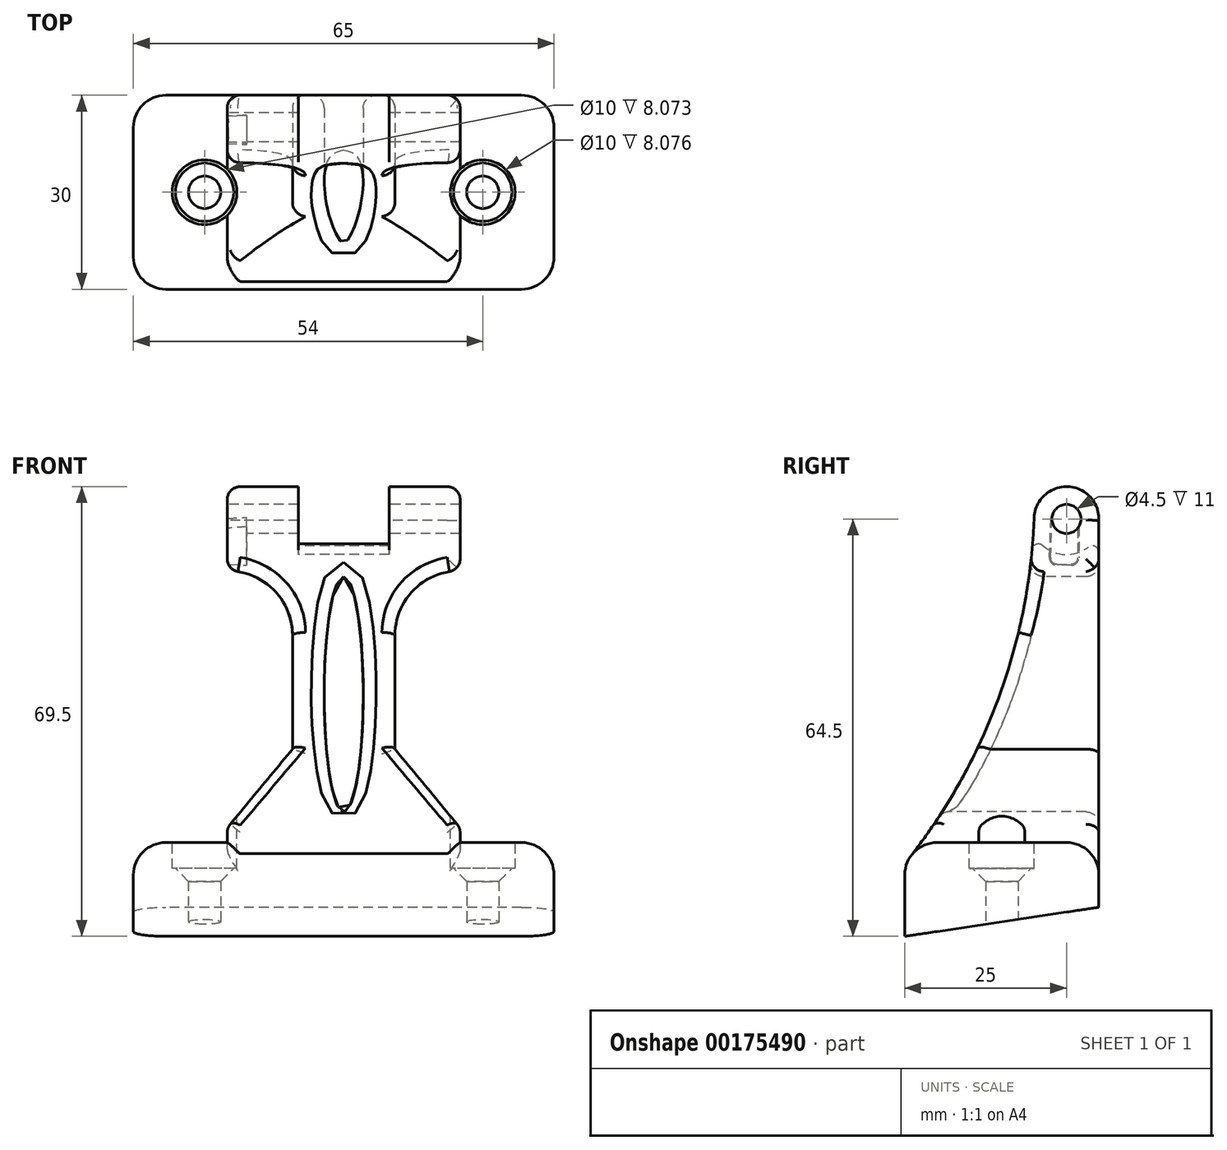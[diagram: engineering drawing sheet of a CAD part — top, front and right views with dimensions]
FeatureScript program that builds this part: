
annotation { "Feature Type Name" : "Feature", "Feature Type Description" : "" }
export const myFeature = defineFeature(function(context is Context, id is Id, definition is map)
    precondition{}
    {
        {
            var Q0;
            Q0=qCreatedBy(makeId("Top.planeOp"),FACE);
            var sketch = newSketch(context, id + "F0", { "sketchPlane" : qUnion([Q0])});
            skLineSegment(sketch, "E0.bottom", {"start": v(-27.5, 15) * mm, "end": v(27.5, 15) * mm});
            skLineSegment(sketch, "E0.top", {"start": v(-27.5, -15) * mm, "end": v(27.5, -15) * mm});
            skLineSegment(sketch, "E0.left", {"start": v(-32.5, 10) * mm, "end": v(-32.5, -10) * mm});
            skLineSegment(sketch, "E0.right", {"start": v(32.5, 10) * mm, "end": v(32.5, -10) * mm});
            skCircle(sketch, "E1", {"center": v(-21.5, 0) * mm, "radius": 2.5 * mm});
            skCircle(sketch, "E2.MirrorC", {"center": v(21.5, 0) * mm, "radius": 2.5 * mm});
            skPoint(sketch, "E3.visualSharp", {"position": v(-32.5, 15) * mm});
            skArc(sketch, "E3.filletArc", {"start": v(-27.5, 15) * mm, "mid": v(-31.04, 13.54) * mm, "end": v(-32.5, 10) * mm});
            skPoint(sketch, "E4.visualSharp", {"position": v(-32.5, -15) * mm});
            skArc(sketch, "E4.filletArc", {"start": v(-32.5, -10) * mm, "mid": v(-31.04, -13.54) * mm, "end": v(-27.5, -15) * mm});
            skPoint(sketch, "E5.visualSharp", {"position": v(32.5, -15) * mm});
            skArc(sketch, "E5.filletArc", {"start": v(27.5, -15) * mm, "mid": v(31.04, -13.54) * mm, "end": v(32.5, -10) * mm});
            skPoint(sketch, "E6.visualSharp", {"position": v(32.5, 15) * mm});
            skArc(sketch, "E6.filletArc", {"start": v(32.5, 10) * mm, "mid": v(31.04, 13.54) * mm, "end": v(27.5, 15) * mm});
            skSolve(sketch);
        }
        {
            var Q0;
            Q0 = qSketchRegion(id + "F0", true);
            extrude(context, id + "F1", {"entities" : qUnion([Q0]), "depth" : 10 * mm, "hasSecondDirection" : true, "secondDirectionOppositeDirection" : true, "secondDirectionDepth" : 5 * mm});
        }
        {
            var Q0;
            Q0=makeQuery(id+"F1.opExtrude","SWEPT_FACE",FACE,{"disambiguationData":[OSD([sQuery(id+"F0.wireOp",EDGE,"E0.left")])]});
            var sketch = newSketch(context, id + "F2", { "sketchPlane" : qUnion([Q0])});
            skLineSegment(sketch, "E7", {"start": v(15, -5) * mm, "end": v(-15, -5) * mm});
            skLineSegment(sketch, "E8", {"start": v(-15, -5) * mm, "end": v(-15, 0) * mm});
            skLineSegment(sketch, "E9", {"start": v(-15, 0) * mm, "end": v(15, -4.5) * mm});
            skLineSegment(sketch, "E10", {"start": v(15, -4.5) * mm, "end": v(15, -5) * mm});
            skSolve(sketch);
        }
        {
            var Q0;
            Q0 = qSketchRegion(id + "F2", true);
            extrude(context, id + "F3", {"entities" : qUnion([Q0]), "operationType" : NewBodyOperationType.REMOVE, "endBound" : BoundingType.THROUGH_ALL, "oppositeDirection" : true, "depth" : 25 * mm});
        }
        {
            var Q0;
            Q0=qCreatedBy(makeId("Right.planeOp"),FACE);
            var sketch = newSketch(context, id + "F4", { "sketchPlane" : qUnion([Q0])});
            skCircle(sketch, "E11", {"center": v(10, 60) * mm, "radius": 2.25 * mm});
            skCircle(sketch, "E12", {"center": v(10, 60) * mm, "radius": 5 * mm});
            skLineSegment(sketch, "E13", {"start": v(21.69, 10) * mm, "end": v(-30.08, 10) * mm, "construction": true});
            skLineSegment(sketch, "E14", {"start": v(15, 59.8) * mm, "end": v(15, 10) * mm});
            skArc(sketch, "E15", {"start": v(-12.48, 10) * mm, "mid": v(0.02, 33.78) * mm, "end": v(5, 60.19) * mm});
            skLineSegment(sketch, "E16", {"start": v(-12.48, 10) * mm, "end": v(15, 10) * mm});
            skSolve(sketch);
        }
        {
            var Q0;
            Q0 = qSketchRegion(id + "F4", true);
            extrude(context, id + "F5", {"entities" : qUnion([Q0]), "operationType" : NewBodyOperationType.ADD, "depth" : 18 * mm, "hasSecondDirection" : true, "secondDirectionOppositeDirection" : true, "secondDirectionDepth" : 18 * mm});
        }
        {
            var Q0;
            Q0=qCreatedBy(makeId("Right.planeOp"),FACE);
            var sketch = newSketch(context, id + "F6", { "sketchPlane" : qUnion([Q0])});
            skCircle(sketch, "E17", {"center": v(10, 60) * mm, "radius": 5.5 * mm});
            skSolve(sketch);
        }
        {
            var Q0;
            Q0 = qSketchRegion(id + "F6", true);
            extrude(context, id + "F7", {"entities" : qUnion([Q0]), "operationType" : NewBodyOperationType.REMOVE, "depth" : 7 * mm, "hasSecondDirection" : true, "secondDirectionOppositeDirection" : true, "secondDirectionDepth" : 7 * mm});
        }
        {
            var Q0;
            Q0=makeQuery(id+"F1.opExtrude","CAP_EDGE",EDGE,{"disambiguationData":[OSD([sQuery(id+"F0.wireOp",EDGE,"E0.right")])],"isStart":false});
            fillet(context, id + "F8", {"entities" : qUnion([Q0]), "radius" : 5 * mm, "tangentPropagation" : true, "allowEdgeOverflow" : false});
        }
        {
            var Q0;
            Q0=makeQuery(id+"F7.boolean.opBoolean","INTERSECT",EDGE,{"derivedFrom":[makeQuery(id+"F5.opExtrude","SWEPT_FACE",FACE,{"disambiguationData":[OSD([sQuery(id+"F4.wireOp",EDGE,"E15")])]}),makeQuery(id+"F7.opExtrude","SWEPT_FACE",FACE,{"disambiguationData":[OSD([sQuery(id+"F6.wireOp",EDGE,"E17")])]})]});
            var Q1;
            Q1=makeQuery(id+"F7.boolean.opBoolean","INTERSECT",EDGE,{"derivedFrom":[makeQuery(id+"F5.opExtrude","SWEPT_FACE",FACE,{"disambiguationData":[OSD([sQuery(id+"F4.wireOp",EDGE,"E14")])]}),makeQuery(id+"F7.opExtrude","SWEPT_FACE",FACE,{"disambiguationData":[OSD([sQuery(id+"F6.wireOp",EDGE,"E17")])]})]});
            fillet(context, id + "F9", {"entities" : qUnion([Q0, Q1]), "radius" : 1 * mm, "tangentPropagation" : true, "allowEdgeOverflow" : false});
        }
        {
            var Q0;
            Q0=makeQuery(id+"F5.opExtrude","CAP_FACE",FACE,{"disambiguationData":[OSD([sQuery(id+"F4.wireOp",EDGE,"E11"),sQuery(id+"F4.wireOp",EDGE,"E12"),sQuery(id+"F4.wireOp",EDGE,"E14"),sQuery(id+"F4.wireOp",EDGE,"E15"),sQuery(id+"F4.wireOp",EDGE,"E16")])],"isStart":true});
            var sketch = newSketch(context, id + "F10", { "sketchPlane" : qUnion([Q0])});
            skLineSegment(sketch, "E18", {"start": v(-7.75, 60.08) * mm, "end": v(-7.52, 54.04) * mm});
            skLineSegment(sketch, "E19", {"start": v(-11.75, 59.88) * mm, "end": v(-11.75, 54) * mm});
            skLineSegment(sketch, "E20", {"start": v(-10.75, 53) * mm, "end": v(-8.52, 53) * mm});
            skLineSegment(sketch, "E21", {"start": v(-7.75, 60.08) * mm, "end": v(-11.75, 59.88) * mm});
            skPoint(sketch, "E22.visualSharp", {"position": v(-11.75, 53) * mm});
            skArc(sketch, "E22.filletArc", {"start": v(-11.75, 54) * mm, "mid": v(-11.45, 53.3) * mm, "end": v(-10.75, 53) * mm});
            skPoint(sketch, "E23.visualSharp", {"position": v(-7.49, 53) * mm});
            skArc(sketch, "E23.filletArc", {"start": v(-8.52, 53) * mm, "mid": v(-7.8, 53.3) * mm, "end": v(-7.52, 54.04) * mm});
            skSolve(sketch);
        }
        {
            var Q0;
            Q0 = qSketchRegion(id + "F10", true);
            extrude(context, id + "F11", {"entities" : qUnion([Q0]), "operationType" : NewBodyOperationType.REMOVE, "oppositeDirection" : true, "depth" : 3 * mm, "hasDraft" : true, "draftAngle" : 3 * degree});
        }
        {
            var Q0;
            Q0=makeQuery(id+"Fu832J7Y8MEkpcE_1.opFillet","SPLIT",FACE,{"disambiguationData":[OD(1.0)],"derivedFrom":makeQuery(id+"F8.opFillet","SPLIT",FACE,{"disambiguationData":[OD(1.0)],"derivedFrom":makeQuery(id+"F1.opExtrude","CAP_FACE",FACE,{"disambiguationData":[OSD([sQuery(id+"F0.wireOp",EDGE,"E0.bottom"),sQuery(id+"F0.wireOp",EDGE,"E0.top"),sQuery(id+"F0.wireOp",EDGE,"E0.left"),sQuery(id+"F0.wireOp",EDGE,"E0.right"),sQuery(id+"F0.wireOp",EDGE,"E1"),sQuery(id+"F0.wireOp",EDGE,"E2.MirrorC"),sQuery(id+"F0.wireOp",EDGE,"E3.filletArc"),sQuery(id+"F0.wireOp",EDGE,"E4.filletArc"),sQuery(id+"F0.wireOp",EDGE,"E5.filletArc"),sQuery(id+"F0.wireOp",EDGE,"E6.filletArc")])],"isStart":false})})});
            var sketch = newSketch(context, id + "F12", { "sketchPlane" : qUnion([Q0])});
            skCircle(sketch, "E24", {"center": v(21.5, 0) * mm, "radius": 5 * mm});
            skCircle(sketch, "E25.MirrorC", {"center": v(-21.5, 0) * mm, "radius": 5 * mm});
            skSolve(sketch);
        }
        {
            var Q0;
            Q0 = qSketchRegion(id + "F12", true);
            extrude(context, id + "F13", {"entities" : qUnion([Q0]), "operationType" : NewBodyOperationType.REMOVE, "flatOperationType" : FlatOperationType.REMOVE, "oppositeDirection" : true, "offsetDistance" : 25 * mm, "depth" : 4 * mm, "hasSecondDirection" : true, "secondDirectionOppositeDirection" : false, "secondDirectionDepth" : 20 * mm, "domain" : OperationDomain.MODEL});
        }
        {
            var Q0;
            Q0=makeQuery(id+"F13.boolean.opBoolean","INTERSECT",EDGE,{"derivedFrom":[makeQuery(id+"F1.opExtrude","SWEPT_FACE",FACE,{"disambiguationData":[OSD([sQuery(id+"F0.wireOp",EDGE,"E1")])]}),makeQuery(id+"F13.opExtrude","CAP_FACE",FACE,{"disambiguationData":[OSD([sQuery(id+"F12.wireOp",EDGE,"E25.MirrorC")])],"isStart":false})]});
            var Q1;
            Q1=makeQuery(id+"F13.boolean.opBoolean","INTERSECT",EDGE,{"derivedFrom":[makeQuery(id+"F1.opExtrude","SWEPT_FACE",FACE,{"disambiguationData":[OSD([sQuery(id+"F0.wireOp",EDGE,"E2.MirrorC")])]}),makeQuery(id+"F13.opExtrude","CAP_FACE",FACE,{"disambiguationData":[OSD([sQuery(id+"F12.wireOp",EDGE,"E24")])],"isStart":false})]});
            chamfer(context, id + "F14", {"entities" : qUnion([Q0, Q1]), "width" : 2 * mm, "tangentPropagation" : true});
        }
        {
            var Q0;
            Q0=makeQuery(id+"F1.opExtrude","SWEPT_FACE",FACE,{"disambiguationData":[OSD([sQuery(id+"F0.wireOp",EDGE,"E0.top")])]});
            var sketch = newSketch(context, id + "F15", { "sketchPlane" : qUnion([Q0])});
            skLineSegment(sketch, "E26", {"start": v(25.2, 52) * mm, "end": v(7.91, 52) * mm});
            skLineSegment(sketch, "E27", {"start": v(7.91, 52) * mm, "end": v(7.91, 24.44) * mm});
            skLineSegment(sketch, "E28", {"start": v(7.91, 24.44) * mm, "end": v(19.1, 10.93) * mm});
            skLineSegment(sketch, "E29", {"start": v(25.2, 52) * mm, "end": v(19.1, 10.93) * mm});
            skLineSegment(sketch, "E30.MirrorCS", {"start": v(-25.2, 52) * mm, "end": v(-7.91, 52) * mm});
            skLineSegment(sketch, "E31.MirrorCS", {"start": v(-25.2, 52) * mm, "end": v(-19.1, 10.93) * mm});
            skLineSegment(sketch, "E32.MirrorCS", {"start": v(-7.91, 24.44) * mm, "end": v(-19.1, 10.93) * mm});
            skLineSegment(sketch, "E33.MirrorCS", {"start": v(-7.91, 52) * mm, "end": v(-7.91, 24.44) * mm});
            skSolve(sketch);
        }
        {
            var Q0;
            Q0 = qSketchRegion(id + "F15", true);
            extrude(context, id + "F16", {"entities" : qUnion([Q0]), "operationType" : NewBodyOperationType.REMOVE, "endBound" : BoundingType.THROUGH_ALL, "oppositeDirection" : true, "depth" : 25 * mm});
        }
        {
            var Q0;
            Q0=makeQuery(id+"F16.boolean.opBoolean","COPY",EDGE,{"derivedFrom":makeQuery(id+"F16.opExtrude","SWEPT_EDGE",EDGE,{"disambiguationData":[OSD([sQuery(id+"F15.wireOp",EDGE,"E26"),sQuery(id+"F15.wireOp",EDGE,"E27")])]})});
            var Q1;
            Q1=makeQuery(id+"F16.boolean.opBoolean","COPY",EDGE,{"derivedFrom":makeQuery(id+"F16.opExtrude","SWEPT_EDGE",EDGE,{"disambiguationData":[OSD([sQuery(id+"F15.wireOp",EDGE,"E30.MirrorCS"),sQuery(id+"F15.wireOp",EDGE,"E33.MirrorCS")])]})});
            fillet(context, id + "F17", {"entities" : qUnion([Q0, Q1]), "radius" : 10 * mm, "tangentPropagation" : true, "allowEdgeOverflow" : false});
        }
        {
            var Q0;
            Q0=makeQuery(id+"F17.opFillet","BLEND_EDGE",EDGE,{"blendedFrom":[makeQuery(id+"F16.boolean.opBoolean","COPY",EDGE,{"derivedFrom":makeQuery(id+"F16.opExtrude","SWEPT_EDGE",EDGE,{"disambiguationData":[OSD([sQuery(id+"F15.wireOp",EDGE,"E26"),sQuery(id+"F15.wireOp",EDGE,"E27")])]})}),makeQuery(id+"F5.opExtrude","SWEPT_FACE",FACE,{"disambiguationData":[OSD([sQuery(id+"F4.wireOp",EDGE,"E15")])]})],"blendedInto":[makeQuery(id+"F5.opExtrude","SWEPT_FACE",FACE,{"disambiguationData":[OSD([sQuery(id+"F4.wireOp",EDGE,"E15")])]})]});
            var Q1;
            Q1=makeQuery(id+"F16.boolean.opBoolean","INTERSECT",EDGE,{"derivedFrom":[makeQuery(id+"F5.opExtrude","SWEPT_FACE",FACE,{"disambiguationData":[OSD([sQuery(id+"F4.wireOp",EDGE,"E15")])]}),makeQuery(id+"F16.opExtrude","SWEPT_FACE",FACE,{"disambiguationData":[OSD([sQuery(id+"F15.wireOp",EDGE,"E28")])]})]});
            var Q2;
            Q2=makeQuery(id+"F16.boolean.opBoolean","INTERSECT",EDGE,{"derivedFrom":[makeQuery(id+"F5.opExtrude","SWEPT_FACE",FACE,{"disambiguationData":[OSD([sQuery(id+"F4.wireOp",EDGE,"E14")])]}),makeQuery(id+"F16.opExtrude","SWEPT_FACE",FACE,{"disambiguationData":[OSD([sQuery(id+"F15.wireOp",EDGE,"E28")])]})]});
            var Q3;
            Q3=makeQuery(id+"F16.boolean.opBoolean","INTERSECT",EDGE,{"derivedFrom":[makeQuery(id+"F5.opExtrude","SWEPT_FACE",FACE,{"disambiguationData":[OSD([sQuery(id+"F4.wireOp",EDGE,"E14")])]}),makeQuery(id+"F16.opExtrude","SWEPT_FACE",FACE,{"disambiguationData":[OSD([sQuery(id+"F15.wireOp",EDGE,"E27")])]})]});
            var Q4;
            Q4=makeQuery(id+"F16.boolean.opBoolean","INTERSECT",EDGE,{"derivedFrom":[makeQuery(id+"F5.opExtrude","CAP_FACE",FACE,{"disambiguationData":[OSD([sQuery(id+"F4.wireOp",EDGE,"E11"),sQuery(id+"F4.wireOp",EDGE,"E12"),sQuery(id+"F4.wireOp",EDGE,"E14"),sQuery(id+"F4.wireOp",EDGE,"E15"),sQuery(id+"F4.wireOp",EDGE,"E16")])],"isStart":false}),makeQuery(id+"F16.opExtrude","SWEPT_FACE",FACE,{"disambiguationData":[OSD([sQuery(id+"F15.wireOp",EDGE,"E26")])]})]});
            var Q5;
            Q5=makeQuery(id+"F17.opFillet","BLEND_EDGE",EDGE,{"blendedFrom":[makeQuery(id+"F16.boolean.opBoolean","COPY",EDGE,{"derivedFrom":makeQuery(id+"F16.opExtrude","SWEPT_EDGE",EDGE,{"disambiguationData":[OSD([sQuery(id+"F15.wireOp",EDGE,"E30.MirrorCS"),sQuery(id+"F15.wireOp",EDGE,"E33.MirrorCS")])]})}),makeQuery(id+"F5.opExtrude","SWEPT_FACE",FACE,{"disambiguationData":[OSD([sQuery(id+"F4.wireOp",EDGE,"E15")])]})],"blendedInto":[makeQuery(id+"F5.opExtrude","SWEPT_FACE",FACE,{"disambiguationData":[OSD([sQuery(id+"F4.wireOp",EDGE,"E15")])]})]});
            var Q6;
            Q6=makeQuery(id+"F17.opFillet","BLEND_EDGE",EDGE,{"blendedFrom":[makeQuery(id+"F16.boolean.opBoolean","COPY",EDGE,{"derivedFrom":makeQuery(id+"F16.opExtrude","SWEPT_EDGE",EDGE,{"disambiguationData":[OSD([sQuery(id+"F15.wireOp",EDGE,"E30.MirrorCS"),sQuery(id+"F15.wireOp",EDGE,"E33.MirrorCS")])]})}),makeQuery(id+"F5.opExtrude","SWEPT_FACE",FACE,{"disambiguationData":[OSD([sQuery(id+"F4.wireOp",EDGE,"E14")])]})],"blendedInto":[makeQuery(id+"F5.opExtrude","SWEPT_FACE",FACE,{"disambiguationData":[OSD([sQuery(id+"F4.wireOp",EDGE,"E14")])]})]});
            var Q7;
            Q7=makeQuery(id+"F16.boolean.opBoolean","INTERSECT",EDGE,{"derivedFrom":[makeQuery(id+"F5.opExtrude","SWEPT_FACE",FACE,{"disambiguationData":[OSD([sQuery(id+"F4.wireOp",EDGE,"E14")])]}),makeQuery(id+"F16.opExtrude","SWEPT_FACE",FACE,{"disambiguationData":[OSD([sQuery(id+"F15.wireOp",EDGE,"E32.MirrorCS")])]})]});
            var Q8;
            Q8=makeQuery(id+"F16.boolean.opBoolean","INTERSECT",EDGE,{"derivedFrom":[makeQuery(id+"F5.opExtrude","SWEPT_FACE",FACE,{"disambiguationData":[OSD([sQuery(id+"F4.wireOp",EDGE,"E15")])]}),makeQuery(id+"F16.opExtrude","SWEPT_FACE",FACE,{"disambiguationData":[OSD([sQuery(id+"F15.wireOp",EDGE,"E32.MirrorCS")])]})]});
            var Q9;
            Q9=makeQuery(id+"F16.boolean.opBoolean","INTERSECT",EDGE,{"derivedFrom":[makeQuery(id+"F5.opExtrude","CAP_FACE",FACE,{"disambiguationData":[OSD([sQuery(id+"F4.wireOp",EDGE,"E11"),sQuery(id+"F4.wireOp",EDGE,"E12"),sQuery(id+"F4.wireOp",EDGE,"E14"),sQuery(id+"F4.wireOp",EDGE,"E15"),sQuery(id+"F4.wireOp",EDGE,"E16")])],"isStart":true}),makeQuery(id+"F16.opExtrude","SWEPT_FACE",FACE,{"disambiguationData":[OSD([sQuery(id+"F15.wireOp",EDGE,"E30.MirrorCS")])]})]});
            fillet(context, id + "F18", {"entities" : qUnion([Q0, Q1, Q2, Q3, Q4, Q5, Q6, Q7, Q8, Q9]), "radius" : 2 * mm, "tangentPropagation" : true, "allowEdgeOverflow" : false});
        }
        {
            var Q0;
            Q0=makeQuery(id+"F16.boolean.opBoolean","INTERSECT",EDGE,{"derivedFrom":[makeQuery(id+"F5.opExtrude","CAP_FACE",FACE,{"disambiguationData":[OSD([sQuery(id+"F4.wireOp",EDGE,"E11"),sQuery(id+"F4.wireOp",EDGE,"E12"),sQuery(id+"F4.wireOp",EDGE,"E14"),sQuery(id+"F4.wireOp",EDGE,"E15"),sQuery(id+"F4.wireOp",EDGE,"E16")])],"isStart":false}),makeQuery(id+"F16.opExtrude","SWEPT_FACE",FACE,{"disambiguationData":[OSD([sQuery(id+"F15.wireOp",EDGE,"E28")])]})]});
            var Q1;
            Q1=makeQuery(id+"F16.boolean.opBoolean","INTERSECT",EDGE,{"derivedFrom":[makeQuery(id+"F5.opExtrude","CAP_FACE",FACE,{"disambiguationData":[OSD([sQuery(id+"F4.wireOp",EDGE,"E11"),sQuery(id+"F4.wireOp",EDGE,"E12"),sQuery(id+"F4.wireOp",EDGE,"E14"),sQuery(id+"F4.wireOp",EDGE,"E15"),sQuery(id+"F4.wireOp",EDGE,"E16")])],"isStart":true}),makeQuery(id+"F16.opExtrude","SWEPT_FACE",FACE,{"disambiguationData":[OSD([sQuery(id+"F15.wireOp",EDGE,"E32.MirrorCS")])]})]});
            var Q2;
            {var subQ0=sQuery(id+"F4.wireOp",EDGE,"E14");var subQ1=sQuery(id+"F4.wireOp",EDGE,"E12");Q2=makeQuery(id+"F16.boolean.opBoolean","SPLIT",EDGE,{"disambiguationData":[TD([makeQuery(id+"F5.opExtrude","SWEPT_FACE",FACE,{"disambiguationData":[OSD([subQ1])]})])],"derivedFrom":makeQuery(id+"F5.opExtrude","CAP_EDGE",EDGE,{"disambiguationData":[OSD([subQ0])],"isStart":true})});}
            var Q3;
            {var subQ0=sQuery(id+"F4.wireOp",EDGE,"E15");var subQ1=sQuery(id+"F4.wireOp",EDGE,"E12");Q3=makeQuery(id+"F16.boolean.opBoolean","SPLIT",EDGE,{"disambiguationData":[TD([makeQuery(id+"F5.opExtrude","SWEPT_FACE",FACE,{"disambiguationData":[OSD([subQ1])]})])],"derivedFrom":makeQuery(id+"F5.opExtrude","CAP_EDGE",EDGE,{"disambiguationData":[OSD([subQ0])],"isStart":true})});}
            var Q4;
            {var subQ0=sQuery(id+"F4.wireOp",EDGE,"E15");var subQ1=sQuery(id+"F4.wireOp",EDGE,"E12");Q4=makeQuery(id+"F16.boolean.opBoolean","SPLIT",EDGE,{"disambiguationData":[TD([makeQuery(id+"F5.opExtrude","SWEPT_FACE",FACE,{"disambiguationData":[OSD([subQ1])]})])],"derivedFrom":makeQuery(id+"F5.opExtrude","CAP_EDGE",EDGE,{"disambiguationData":[OSD([subQ0])],"isStart":false})});}
            fillet(context, id + "F19", {"entities" : qUnion([Q0, Q1, Q2, Q3, Q4]), "radius" : 2 * mm, "tangentPropagation" : true, "allowEdgeOverflow" : false});
        }
        {
            var Q0;
            Q0=makeQuery(id+"F1.opExtrude","SWEPT_FACE",FACE,{"disambiguationData":[OSD([sQuery(id+"F0.wireOp",EDGE,"E0.top")])]});
            var sketch = newSketch(context, id + "F20", { "sketchPlane" : qUnion([Q0])});
            skEllipse(sketch, "E34", {"center": v(0, 32.92) * mm, "majorRadius": 18.17 * mm, "minorRadius": 3.02 * mm, "majorAxis": v(0, 1)});
            skSolve(sketch);
        }
        {
            var Q0;
            Q0 = qSketchRegion(id + "F20", true);
            extrude(context, id + "F21", {"entities" : qUnion([Q0]), "operationType" : NewBodyOperationType.REMOVE, "endBound" : BoundingType.THROUGH_ALL, "oppositeDirection" : true, "depth" : 25 * mm});
        }
        {
            var Q0;
            Q0=makeQuery(id+"F21.boolean.opBoolean","INTERSECT",EDGE,{"derivedFrom":[makeQuery(id+"F5.opExtrude","SWEPT_FACE",FACE,{"disambiguationData":[OSD([sQuery(id+"F4.wireOp",EDGE,"E15")])]}),makeQuery(id+"F21.opExtrude","SWEPT_FACE",FACE,{"disambiguationData":[OSD([sQuery(id+"F20.wireOp",EDGE,"E34")])]})]});
            var Q1;
            Q1=makeQuery(id+"F21.boolean.opBoolean","INTERSECT",EDGE,{"derivedFrom":[makeQuery(id+"F5.opExtrude","SWEPT_FACE",FACE,{"disambiguationData":[OSD([sQuery(id+"F4.wireOp",EDGE,"E14")])]}),makeQuery(id+"F21.opExtrude","SWEPT_FACE",FACE,{"disambiguationData":[OSD([sQuery(id+"F20.wireOp",EDGE,"E34")])]})]});
            fillet(context, id + "F22", {"entities" : qUnion([Q0, Q1]), "radius" : 2 * mm, "tangentPropagation" : true, "allowEdgeOverflow" : false});
        }
    });
